# Revit family: 60-164-812_graa_trestuktue_simplified
name_source: partatom
category: Generic Models
units: mm (PartAtom-declared; Revit-internal decimal feet)

## family parameters
Always vertical = Yes
Can host rebar = No
Cut with Voids When Loaded = No
Part Type = Normal
Room Calculation Point = No
Round Connector Dimension = Use Diameter
Shared = No
Work Plane-Based = No

## types (1)
- Type 1
    Artnr_graa_trestuktue_simplified = 60-164-831
    Default Elevation = 0 mm  [stored 0 ft]
    Description_graa_trestuktue_simplified = Sandelekebord trekant trippel
    Number = 21065
    Number_graa_trestuktue_simplified = 21065
    PartName_graa_trestuktue_simplified = Sandelekebord trekant trippel
    Revision = 0
    Revision_graa_trestuktue_simplified = 0

note: [stored X ft] marks values corroborated as IEEE doubles in the binary element streams (Revit-internal decimal feet)

## geometry (parser evidence)
native form markers: Sweep x14
no freeform markers — native parametric forms only
